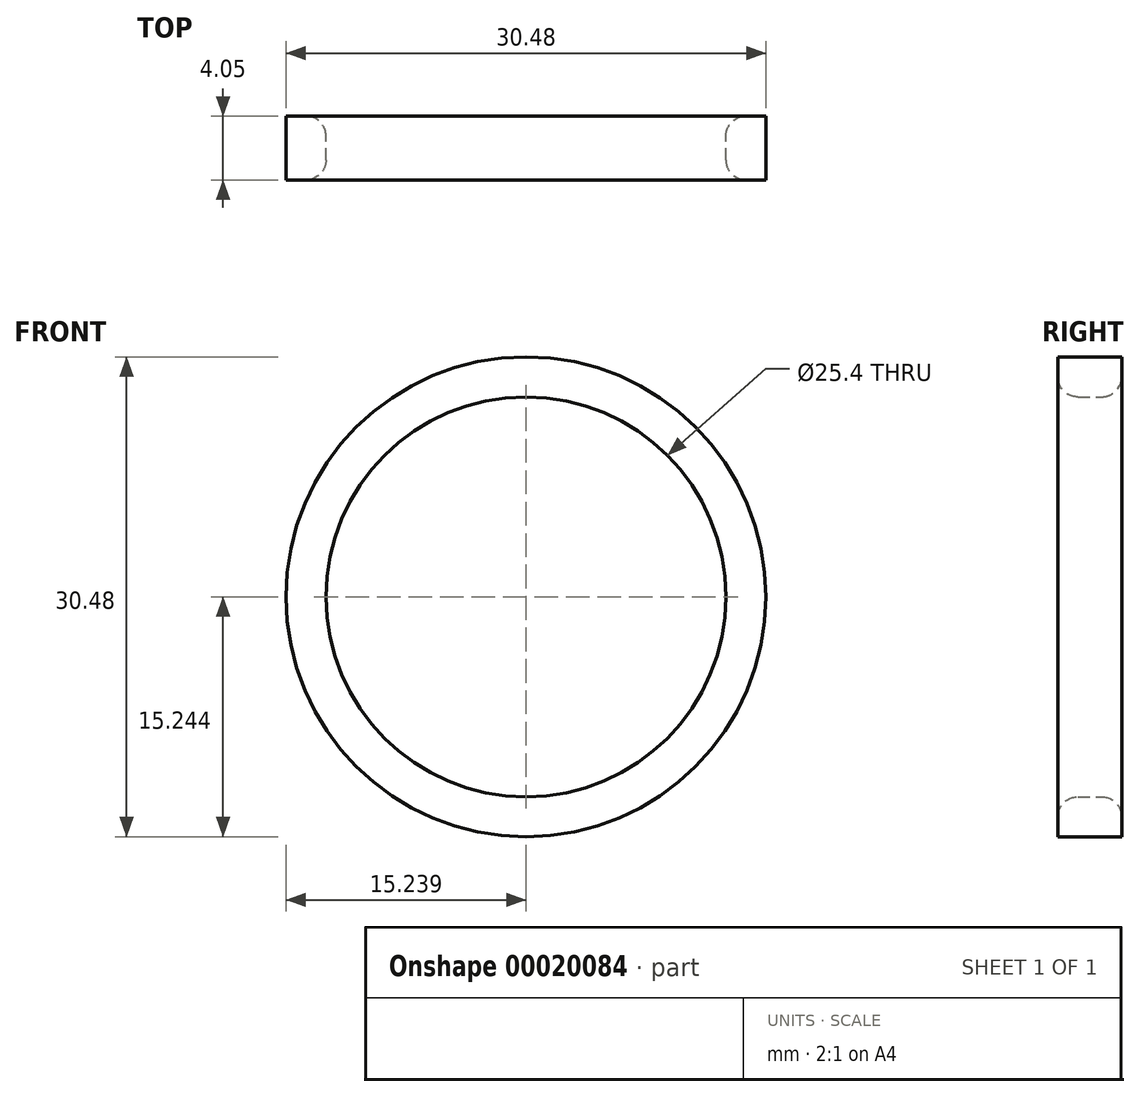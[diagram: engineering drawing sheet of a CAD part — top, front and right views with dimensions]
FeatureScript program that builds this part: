
annotation { "Feature Type Name" : "Feature", "Feature Type Description" : "" }
export const myFeature = defineFeature(function(context is Context, id is Id, definition is map)
    precondition{}
    {
        {
            var Q0;
            Q0=qCreatedBy(makeId("Front.planeOp"),FACE);
            var sketch = newSketch(context, id + "F0", { "sketchPlane" : qUnion([Q0])});
            skCircle(sketch, "E0", {"center": v(-2.36, -22.86) * mm, "radius": 12.7 * mm});
            skCircle(sketch, "E1.0", {"center": v(-2.36, -22.86) * mm, "radius": 15.24 * mm});
            skSolve(sketch);
        }
        {
            var Q0;
            Q0=makeQuery(id+"F0.imprint","IMPRINT",FACE,{"disambiguationData":[TD([[makeQuery(id+"F0.imprint","IMPRINT",EDGE,{"derivedFrom":sQuery(id+"F0.wireOp",EDGE,"E0")}),-1.0]])]});
            extrude(context, id + "F1", {"entities" : qUnion([Q0]), "depth" : 4.05 * mm});
        }
        {
            var Q0;
            Q0=makeQuery(id+"F1.opExtrude","SWEPT_FACE",FACE,{"disambiguationData":[OSD([sQuery(id+"F0.wireOp",EDGE,"E0")])]});
            var Q1;
            Q1=makeQuery(id+"F1.opExtrude","CAP_EDGE",EDGE,{"disambiguationData":[OSD([sQuery(id+"F0.wireOp",EDGE,"E0")])],"isStart":true});
            fillet(context, id + "F2", {"entities" : qUnion([Q0, Q1]), "radius" : 1.27 * mm, "tangentPropagation" : true, "allowEdgeOverflow" : false});
        }
    });
